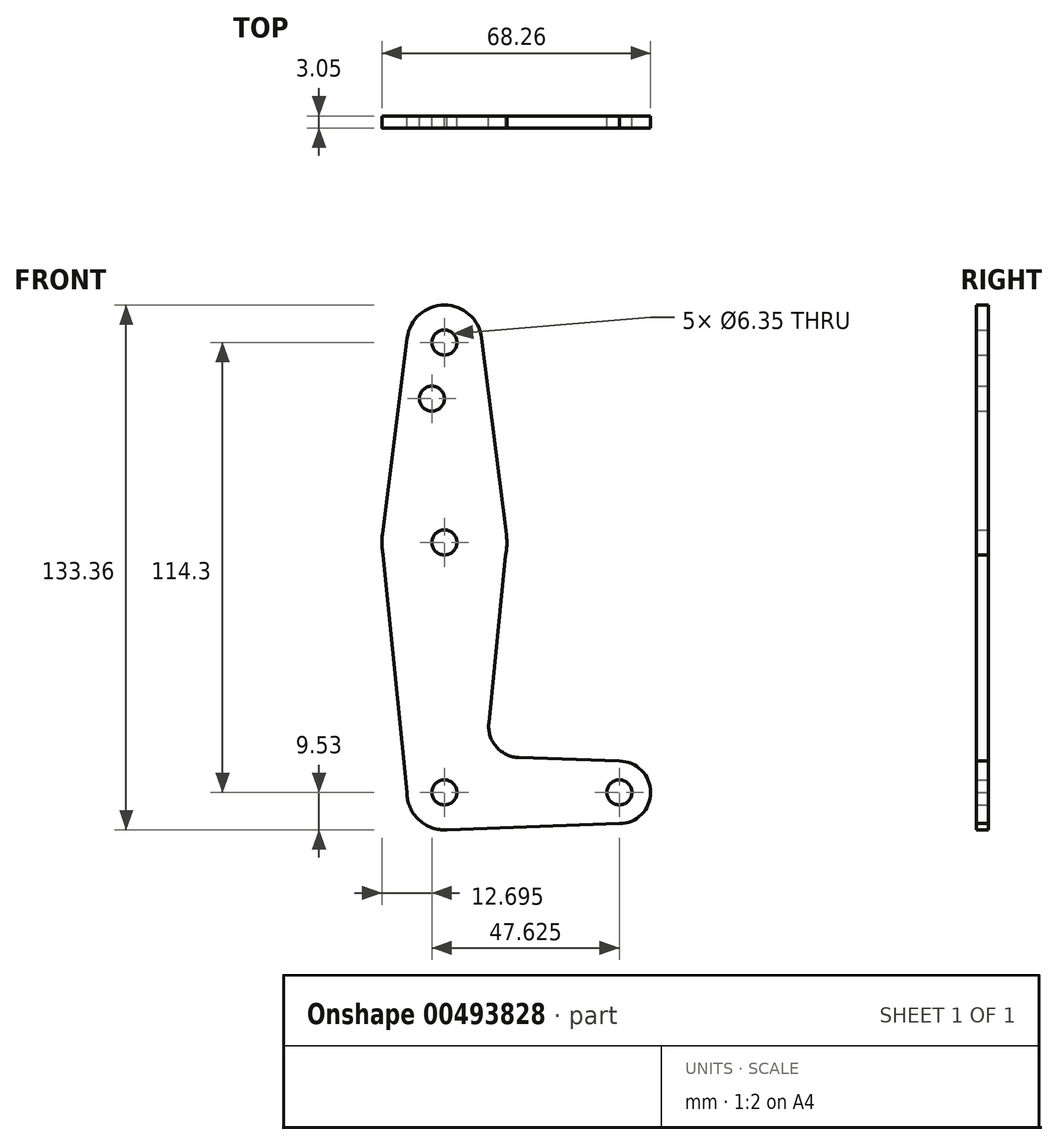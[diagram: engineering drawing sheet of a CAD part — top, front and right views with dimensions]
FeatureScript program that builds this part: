
annotation { "Feature Type Name" : "Feature", "Feature Type Description" : "" }
export const myFeature = defineFeature(function(context is Context, id is Id, definition is map)
    precondition{}
    {
        {
            var Q0;
            Q0=qCreatedBy(makeId("Front.planeOp"),FACE);
            var sketch = newSketch(context, id + "F0", { "sketchPlane" : qUnion([Q0])});
            skLineSegment(sketch, "E0", {"start": v(0, 0) * mm, "end": v(0, 114.3) * mm, "construction": true});
            skLineSegment(sketch, "E1", {"start": v(0, 0) * mm, "end": v(44.45, 0) * mm, "construction": true});
            skCircle(sketch, "E2", {"center": v(0, 114.3) * mm, "radius": 9.53 * mm});
            skCircle(sketch, "E3", {"center": v(0, 63.5) * mm, "radius": 15.88 * mm});
            skCircle(sketch, "E4", {"center": v(0, 0) * mm, "radius": 9.53 * mm});
            skCircle(sketch, "E5", {"center": v(44.45, 0) * mm, "radius": 7.94 * mm});
            skLineSegment(sketch, "E6", {"start": v(9.45, 115.5) * mm, "end": v(15.75, 65.48) * mm});
            skLineSegment(sketch, "E7", {"start": v(-9.45, 115.5) * mm, "end": v(-15.75, 65.48) * mm});
            skLineSegment(sketch, "E8", {"start": v(-15.56, 60.34) * mm, "end": v(-9.52, 0) * mm});
            skLineSegment(sketch, "E9", {"start": v(15.56, 60.34) * mm, "end": v(11.28, 17.59) * mm});
            skLineSegment(sketch, "E10", {"start": v(18.91, 8.85) * mm, "end": v(44.45, 7.94) * mm});
            skLineSegment(sketch, "E11", {"start": v(0, -9.52) * mm, "end": v(44.45, -7.94) * mm});
            skCircle(sketch, "E12", {"center": v(-3.18, 100.03) * mm, "radius": 3.18 * mm});
            skCircle(sketch, "E13", {"center": v(0, 63.5) * mm, "radius": 3.18 * mm});
            skCircle(sketch, "E14", {"center": v(0, 114.3) * mm, "radius": 3.18 * mm});
            skCircle(sketch, "E15", {"center": v(0, 0) * mm, "radius": 3.18 * mm});
            skCircle(sketch, "E16", {"center": v(44.45, 0) * mm, "radius": 3.18 * mm});
            skPoint(sketch, "E17.newPointB", {"position": v(9.52, 0) * mm});
            skArc(sketch, "E17.filletArc", {"start": v(11.28, 17.59) * mm, "mid": v(13.2, 11.57) * mm, "end": v(18.91, 8.85) * mm});
            skSolve(sketch);
        }
        {
            var Q0;
            Q0 = qSketchRegion(id + "F0", true);
            extrude(context, id + "F1", {"entities" : qUnion([Q0]), "depth" : 3.05 * mm});
        }
    });
